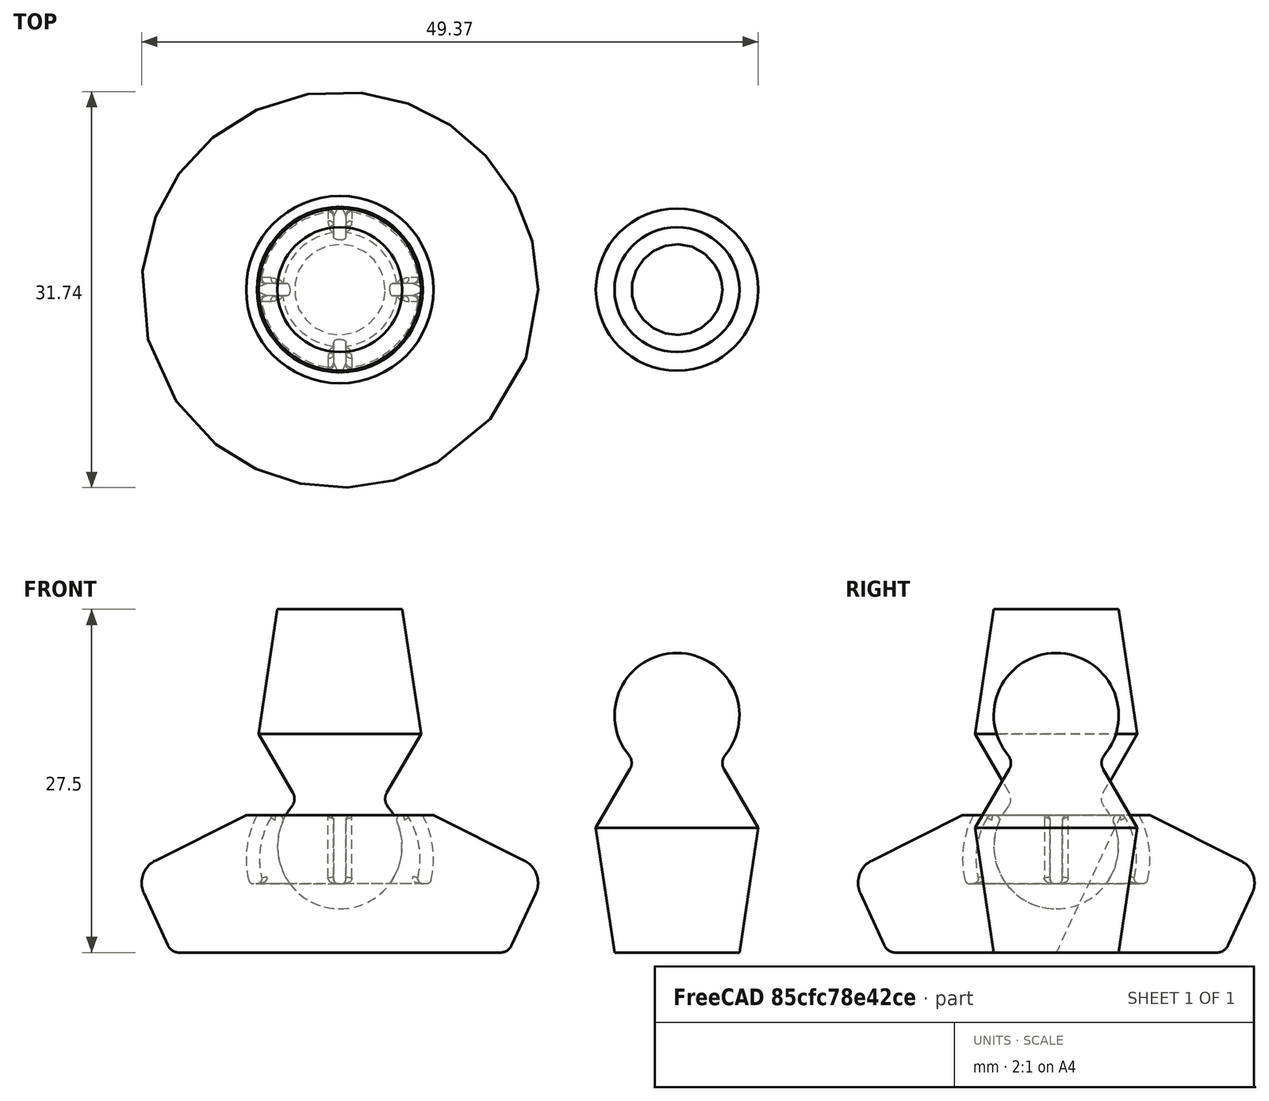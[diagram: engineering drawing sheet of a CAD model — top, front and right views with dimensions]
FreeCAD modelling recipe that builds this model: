
FCSTD DOCUMENT  (FreeCAD 0.14R3703 (Git))
Label: Eames Lounge Foot v4
License: CC-BY 3.0
LicenseURL: http://creativecommons.org/licenses/by/3.0/
objects: PartDesign::Fillet×6, Part::Cone×4, Part::MultiFuse×4, Part::Sphere×4, Part::Cylinder×3, Part::Cut×3, Drawing::FeaturePage×1, Part::Feature×1
note: 25 computed .brp shape members not serialized (recipe doc carries the construction recipe); baked Part::Feature solids carry a one-line shape summary decoded from their .brp

FEATURE [Part::Cone] Cone002  label="Cone1"
  Angle = 360
  Height = 6.5
  Radius1 = 13.5
  Radius2 = 16.5
FEATURE [Part::Cone] Cone003  label="Cone2"
  Angle = 360
  Height = 4.5
  Placement = pos=(0,0,6.5) rot=(0,0,1;0rad)
  Radius1 = 16.5
  Radius2 = 7.5
FEATURE [Part::MultiFuse] Fusion001  label="Foot Uncut"
  Shapes = -> [Cone002,Cone003]
FEATURE [Part::Sphere] Sphere002
  Angle1 = -90
  Angle2 = 90
  Angle3 = 360
  Placement = pos=(0,0,7) rot=(0,0,1;0rad)
  Radius = 7.5
FEATURE [Part::Cylinder] Cylinder
  Angle = 360
  Height = 6
  Placement = pos=(0,0,-1) rot=(0,0,1;0rad)
  Radius = 10
FEATURE [Part::Sphere] Sphere004
  Angle1 = -90
  Angle2 = 90
  Angle3 = 360
  Placement = pos=(0,0,7) rot=(0,0,1;0rad)
  Radius = 6.5
FEATURE [Part::Cylinder] Cylinder001
  Angle = 360
  Height = 1
  Placement = pos=(-0.5,0,7) rot=(0,1,0;1.5708rad)
  Radius = 6.5
FEATURE [Part::Cylinder] Cylinder002
  Angle = 360
  Height = 1
  Placement = pos=(0,0.5,7) rot=(1,0,0;1.5708rad)
  Radius = 6.5
FEATURE [Part::Cut] Cut001
  Base = -> Sphere002
  Tool = -> Sphere004
FEATURE [Part::MultiFuse] Fusion002
  Shapes = -> [Cylinder001,Cylinder002,Cut001]
FEATURE [Part::Sphere] Sphere001
  Angle1 = -90
  Angle2 = 90
  Angle3 = 360
  Placement = pos=(0,0,8) rot=(0,0,1;0rad)
  Radius = 5
FEATURE [Part::Cut] Cut  label="Cutout unfilleted"
  Base = -> Fusion002
  Tool = -> Cylinder
FEATURE [PartDesign::Fillet] Fillet  label="Cutout"
  Base = -> Cut [Edge2,Edge4,Edge5,Edge6,Edge7,Edge8,Edge9,Edge10,Edge11,Edge12,Edge13,Edge14,Edge15]
  Radius = 0.4
FEATURE [PartDesign::Fillet] Fillet001
  Base = -> Fillet [Edge58,Edge55,Edge53,Edge50,Edge52,Edge60,Edge61,Edge57]
  Radius = 0.4
FEATURE [Part::MultiFuse] Fusion003
  Placement = pos=(0,0,0.5) rot=(0,0,1;0rad)
  Shapes = -> [Fillet001,Sphere001]
FEATURE [Part::Cut] Cut002  label="Foot untilleted"
  Base = -> Fusion001
  Tool = -> Fusion003
FEATURE [Part::Cone] Cone001
  Angle = 360
  Height = 10
  Placement = pos=(0,0,17) rot=(0,0,1;0rad)
  Radius1 = 6.5
  Radius2 = 5
FEATURE [Part::Sphere] Sphere
  Angle1 = -90
  Angle2 = 90
  Angle3 = 360
  Placement = pos=(0,0,8) rot=(0,0,1;0rad)
  Radius = 5
FEATURE [PartDesign::Fillet] Fillet008
  Base = -> Cut002 [Edge44,Edge106,Edge107,Edge108,Edge109,Edge104,Edge40,Edge97,Edge101,Edge87,Edge102,Edge99,Edge124,Edge125,Edge126,Edge127,Edge121,Edge54,Edge115,Edge112,Edge49,Edge116,Edge117,Edge118]
  Radius = 0.4
FEATURE [PartDesign::Fillet] Fillet009
  Base = -> Fillet008 [Edge231]
  Radius = 2
FEATURE [PartDesign::Fillet] Fillet010  label="Foot"
  Base = -> Fillet009 [Edge8]
  Radius = 1
FEATURE [Drawing::FeaturePage] Page
  EditableTexts = AUTHOR NAME | CREATION DATE | SUPERVISOR NAME | CHECK DATE | SCALE | WEIGHT | NUMBER | SHEET | TITLE | SUBTITLE
  Template = /Applications/FreeCAD.app/Contents/data/Mod/Drawing/Templates/A3_Landscape.svg
FEATURE [Part::Cone] Cone
  Angle = 360
  Height = 6
  Placement = pos=(0,0,11) rot=(0,0,1;0rad)
  Radius1 = 3
  Radius2 = 6.5
FEATURE [Part::MultiFuse] Fusion  label="Shaft Unfilleted"
  Placement = pos=(0,0,0.5) rot=(0,0,1;0rad)
  Shapes = -> [Sphere,Cone001,Cone]
FEATURE [PartDesign::Fillet] Fillet005  label="Shaft In Place"
  Base = -> Fusion [Edge5]
  Placement = pos=(0,0,0.5) rot=(0,0,1;0rad)
  Radius = 1
FEATURE [Part::Feature] Fillet011  label="Shaft adjacent"
  Placement = pos=(27,0,27) rot=(1,0,0;3.14159rad)
  shape: bbox 13 x 13 x 24 mm, 5 faces (baked)
